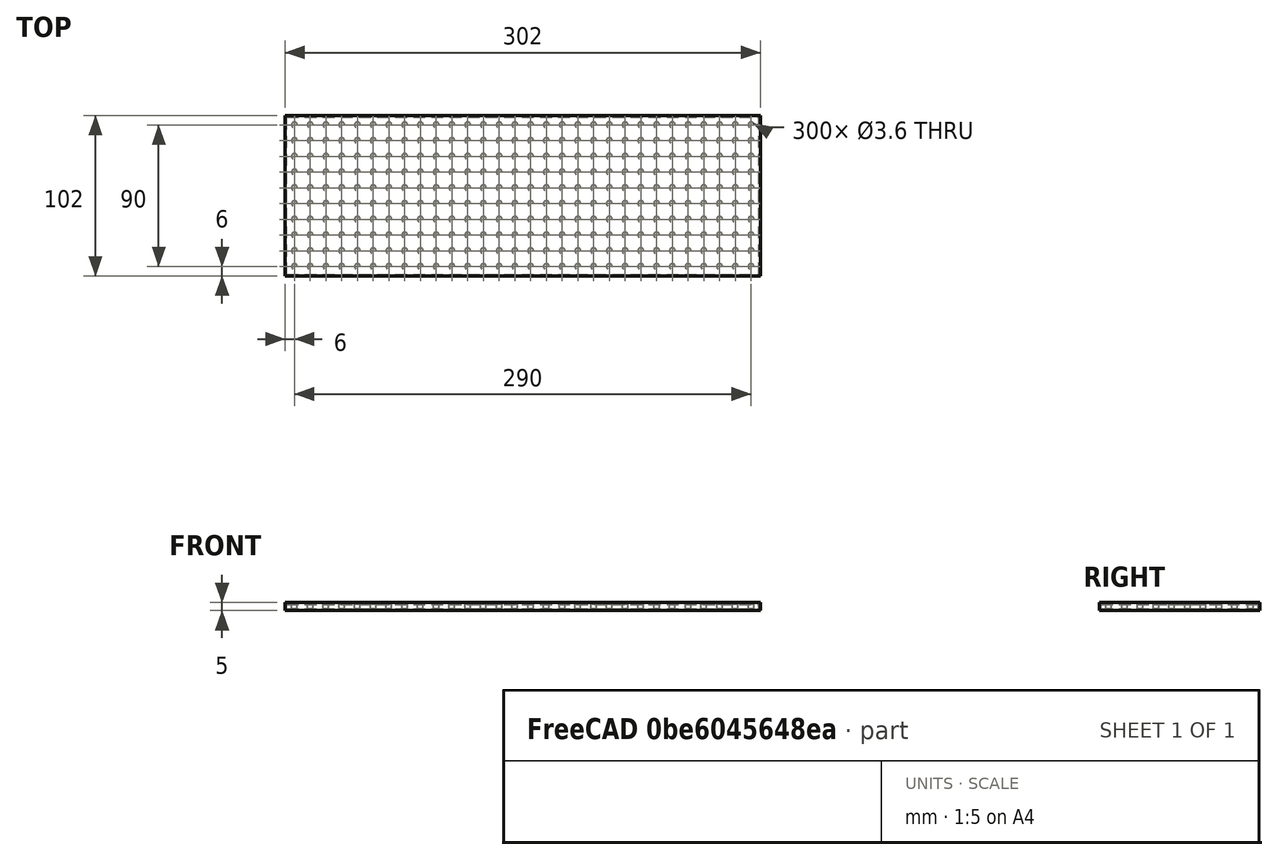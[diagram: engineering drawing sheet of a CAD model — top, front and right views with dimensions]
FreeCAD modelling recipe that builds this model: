
FCSTD DOCUMENT  (FreeCAD 0.18.4R)
Label: hole_plate1
License: All rights reserved
LicenseURL: http://en.wikipedia.org/wiki/All_rights_reserved
objects: Path::FeaturePython×4, Part::FeaturePython×3, Part::Box×1, Spreadsheet::Sheet×1, Part::Cylinder×1, Part::Cut×1, App::FeaturePython×1, App::DocumentObjectGroup×1, Path::FeatureCompoundPython×1
note: 7 computed .brp shape members not serialized (recipe doc carries the construction recipe); baked Part::Feature solids carry a one-line shape summary decoded from their .brp

FEATURE [Part::Box] Box  label="hole plate cube"
  AttacherType = Attacher::AttachEngine3D
  Height = 3
  Length = 300
  Width = 100
  expr: Length = p.plate_x
  expr: Width = p.plate_y
FEATURE [Spreadsheet::Sheet] Spreadsheet  label="p"
  cells = A1=hole_r; B1(hole_r)=1.8; A2=plate_hole_dist; B2(plate_hole_dist)=10; A3=plate_x; B3(plate_x)=300; A4=plate_y; B4(plate_y)=100
FEATURE [Part::Cylinder] Cylinder  label="the hole"
  Angle = 360
  AttacherType = Attacher::AttachEngine3D
  Height = 10
  Radius = 1.8
  expr: Radius = p.hole_r
FEATURE [Part::FeaturePython] Array  label="hole array"  # Draft array (typed FeaturePython)
  Angle = 360
  ArrayType = 0
  Axis = (0,0,1)
  Base = -> Cylinder
  Center = (0,0,0)
  Fuse = false
  IntervalAxis = (0,0,0)
  IntervalX = (10,0,0)
  IntervalY = (0,10,0)
  IntervalZ = (0,0,1)
  NumberPolar = 1
  NumberX = 30
  NumberY = 10
  NumberZ = 1
  Placement = pos=(5,5,0) rot=(0,0,1;0rad)
  expr: Placement.Base.y = p.plate_hole_dist / 2
  expr: Placement.Base.x = p.plate_hole_dist / 2
  expr: IntervalX.x = p.plate_hole_dist
  expr: NumberY = floor(p.plate_y / p.plate_hole_dist)
  expr: NumberX = floor(p.plate_x / p.plate_hole_dist)
FEATURE [Part::Cut] Cut  label="hole plate cut"
  Base = -> Box
  Tool = -> Array
FEATURE [App::FeaturePython] SetupSheet  # Path/CAM operation (typed FeaturePython)
  ClearanceHeightExpression = OpStockZMax+SetupSheet.ClearanceHeightOffset
  ClearanceHeightOffset = 0
  FinalDepthExpression = OpFinalDepth
  HorizRapid = 100
  SafeHeightExpression = OpStockZMax+SetupSheet.SafeHeightOffset
  SafeHeightOffset = 0
  StartDepthExpression = OpStartDepth
  StepDownExpression = OpToolDiameter
  VertRapid = 100
FEATURE [Part::FeaturePython] Clone  label="Model-hole plate cut"  # Draft clone (typed FeaturePython)
  AttacherType = Attacher::AttachEngine3D
  Fuse = false
  Objects = -> [Cut]
  PathResource = Model
  Scale = (1,1,1)
FEATURE [App::DocumentObjectGroup] Model
  Group = -> [Clone]
FEATURE [Path::FeaturePython] T3__laser  label="T3: laser"  # Path/CAM operation (typed FeaturePython)
  HorizFeed = 0.5
  HorizRapid = 100
  SpindleDir = 0
  SpindleSpeed = 1000
  ToolNumber = 3
  VertFeed = 0.5
  VertRapid = 100
  expr: VertRapid = SetupSheet.VertRapid
  expr: HorizRapid = SetupSheet.HorizRapid
FEATURE [Part::FeaturePython] Stock  # WARN: FeaturePython — macro-defined, semantics opaque (R4)
  Base = -> Model
  ExtXneg = 1
  ExtXpos = 1
  ExtYneg = 1
  ExtYpos = 1
  ExtZneg = 1
  ExtZpos = 1
  StockType = FromBase
FEATURE [Path::FeaturePython] Contour  # Path/CAM operation (typed FeaturePython)
  Active = true
  AreaParams:
    Tolerance = 1e-07
    FitArcs = True
    Simplify = False
    CleanDistance = 0.0
    Accuracy = 0.01
    Unit = 1.0
    MinArcPoints = 4
    MaxArcPoints = 100
    ClipperScale = 10000000.0
    Fill = 0
    Coplanar = 2
    Reorient = True
    Outline = False
    Explode = False
    OpenMode = 0
    Deflection = 0.01
    SubjectFill = 0
    ClipFill = 0
    Offset = 0.1
    ExtraPass = 0
    Stepover = 0.0
    LastStepover = 0.0
    JoinType = 0
    EndType = 0
    MiterLimit = 2.0
    RoundPrecision = 0.0
    PocketMode = 0
    ToolRadius = 1.0
    PocketExtraOffset = 0.0
    PocketStepover = 0.0
    PocketLastStepover = 0.0
    FromCenter = False
    Angle = 45.0
    AngleShift = 0.0
    Shift = 0.0
    Thicken = False
    SectionCount = -1
    Stepdown = 1.0
    SectionOffset = 0.0
    SectionTolerance = 1e-06
    SectionMode = 2
    Project = False
  ClearanceHeight = 1
  Direction = 0
  FinalDepth = 0
  JoinType = 0
  MiterLimit = 0.1
  OffsetExtra = 0
  OpFinalDepth = -1
  OpStartDepth = 4
  OpStockZMax = 4
  OpStockZMin = -1
  OpToolDiameter = 0.2
  PathParams = {'orientation': 1, 'feedrate': 0.5, 'feedrate_v': 0.5, 'verbose': True, 'resume_height': 1.0, 'retraction': 1.0, 'return_end': True, 'preamble': False}
  SafeHeight = 1
  Side = 0
  StartDepth = 0.1
  StartPoint = (0,0,0)
  StepDown = 0.2
  ToolController = -> T3__laser
  UseComp = true
  UseStartPoint = false
FEATURE [Path::FeaturePython] Engrave  # Path/CAM operation (typed FeaturePython)
  Active = true
  Base = -> [Clone]
  ClearanceHeight = 1
  FinalDepth = 0
  OpFinalDepth = 2.8
  OpStartDepth = 3
  OpStockZMax = 4
  OpStockZMin = -1
  OpToolDiameter = 0.2
  SafeHeight = 1
  StartDepth = 0.1
  StartVertex = 0
  StepDown = 0.2
  ToolController = -> T3__laser
  expr: StepDown = OpToolDiameter
FEATURE [Path::FeatureCompoundPython] Operations  # Path/CAM operation (typed FeaturePython)
  Group = -> [Contour,Engrave]
  UsePlacements = false
FEATURE [Path::FeaturePython] Job  label="hole plate job"  # Path/CAM operation (typed FeaturePython)
  GeometryTolerance = 0.01
  Model = -> Model
  Operations = -> Operations
  PostProcessor = 1
  PostProcessorOutputFile = <userpath>/work/roborep/freecad/hole_plate/hole_plate.gcode
  SetupSheet = -> SetupSheet
  Stock = -> Stock
  ToolController = -> [T3__laser]
